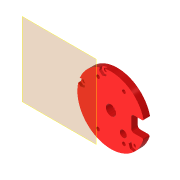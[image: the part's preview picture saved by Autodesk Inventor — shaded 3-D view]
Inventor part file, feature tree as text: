
AUTODESK INVENTOR PART (.ipt)
format: ipt  version: 2022 (Build 260153000, 153)  size: 319,488 bytes
history: native  units: in
note: dims shown in document units (in); Inventor stores cm internally (conversion verified against a paired STEP export)
features: reference x11, extrude x8, sketch x8, other x6, plane x4, chamfer x1
ambient origin geometry x8: Origin, YZ Plane, XZ Plane, XY Plane, X Axis, Y Axis, Z Axis, Center Point
bodies: Solid1 (feature_tree)
feature tree (38):
  plane  "Work Plane1"
  extrude  "Extrusion1"  Depth=0.1969in
  extrude  "Extrusion2"  Depth=1.0in
  plane  "Arbeitsebene4"
  extrude  "Extrusion5"  TaperAngle=0.0deg  [1 undecoded]
  plane  "Arbeitsebene3"
  extrude  "Extrusion6"  Depth=0.1102in
  plane  "Arbeitsebene2"
  extrude  "Extrusion7"  Depth=0.0787in
  extrude  "Extrusion10"  Depth=0.0394in TaperAngle=0.0deg
  extrude  "Extrusion11"  Depth=0.3937in
  chamfer  "Fase3"  Distance=0.2362in
  extrude  "Extrusion12"  Depth=0.2165in
  sketch  "Sketch1"  dims[d0=0.1969in d1=0.0in d2=0.315in]
  reference  "Reference1"
  reference  "Reference2"
  reference  "Reference3"
  reference  "Reference4"
  reference  "Reference5"
  reference  "Reference6"
  reference  "Reference7"
  reference  "Reference8"
  sketch  "Sketch2"  dims[d3=0.311in d4=1.0in d5=-0.0137in]
  sketch  "Sketch7"  dims[d30=0.1102in d31=0.0in d32=0.0in]
  sketch  "Sketch8"  dims[d33=0.1102in d34=0.1102in]
  sketch  "Sketch9"  dims[d35=0.0in d36=0.0in d37=0.0787in]
  sketch  "Skizze12"  dims[d38=0.0004in d39=0.0in d51=0.0394in d52=0.0in]
  sketch  "Skizze13"  dims[d53=0.2638in d54=0.3937in d55=0.2362in d56=0.0in]
  sketch  "Skizze14"  dims[d57=0.0591in d58=0.0787in d59=45.0deg d60=0.2165in d61=0.2165in d62=0.2165in d63=0.0787in d64=0.0in]
  reference  "Referenz27"
  reference  "Referenz28"
  reference  "Referenz29"
  other  "Assembly1"
  other  "Assembly_MANATEE_V0_Manatee_middle2_v0_18:1"
  other  "Matchboxscope_v1.iam"
  other  "DIN 912 - ersetzt durch DIN EN ISO 4762 M3 x 25:2"
  other  "DIN 912 - ersetzt durch DIN EN ISO 4762 M3 x 25:1"
  other  "DIN 912 - ersetzt durch DIN EN ISO 4762 M3 x 25:3"
note: 1 required parameter value undecoded (feature->parameter linkage not recoverable at this tier; creation-order binding heuristic only, values carry confidence <= 0.55)
